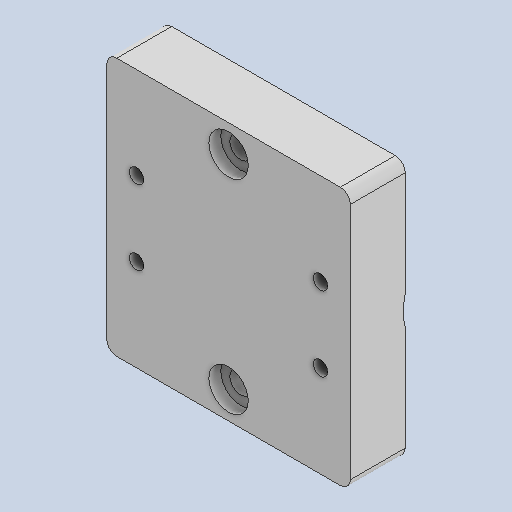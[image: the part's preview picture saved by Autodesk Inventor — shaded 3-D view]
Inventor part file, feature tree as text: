
AUTODESK INVENTOR PART (.ipt)
format: ipt  version: 2024.2 (Build 282272000, 272)  size: 184,320 bytes
history: native  units: in
note: dims shown in document units (in); Inventor stores cm internally (conversion verified against a paired STEP export)
features: hole x3, sketch x3, extrude x2, fillet x1
ambient origin geometry x8: Origin, YZ Plane, XZ Plane, XY Plane, X Axis, Y Axis, Z Axis, Center Point
bodies: Solid1 (feature_tree)
feature tree (9):
  extrude  "Extrusion1"  Depth=2.0472in
  hole  "Hole1"  [1 undecoded]
  fillet  "Fillet1"  Radius=0.435in
  extrude  "Extrusion3"  Depth=0.0984in
  hole  "Hole6"  [1 undecoded]
  hole  "Hole7"  [1 undecoded]
  sketch  "Sketch7"  dims[d0=2.0472in d1=1.0236in]
  sketch  "Sketch11"  dims[d2=1.9291in d3=0.9646in d4=0.435in d5=0.0in]
  sketch  "Sketch12"  dims[d13=0.2165in d14=0.8071in d15=0.2165in d16=0.8071in d17=0.1695in d18=0.224in d19=0.3125in d20=0.0945in d21=0.5635in d22=0.4843in d23=0.0in d40=0.0787in d57=1.0in d58=0.4862in d59=1.9685in d60=0.0in d98=0.8858in d99=0.5906in d100=0.5906in d101=0.8858in d102=0.5906in d103=0.5906in d104=0.2781in d106=0.0793in d107=0.1772in d108=0.1575in d109=0.0787in d110=90.0deg d111=0.2992in d112=0.8108in d115=0.5906in d117=0.1575in d118=0.2953in d119=0.1142in d120=0.2362in d121=0.2165in d122=0.0984in d123=0.5635in d124=0.315in d125=0.8108in d126=1.7717in d127=0.5906in d128=0.1575in d129=0.2953in]
note: 3 required parameter values undecoded (feature->parameter linkage not recoverable at this tier; creation-order binding heuristic only, values carry confidence <= 0.55)
